# Revit family: 81MEJE-81MGJE-81MFJE-81MHJE_MC Chair_Mesh Seat No Pad Back With Armrest Silver Frame Black Shell_1
name_source: partatom
category: Furniture
revit_build: Autodesk Revit 2017 (Build: 20160225_1515(x64)
units: mm (PartAtom-declared; Revit-internal decimal feet)

## family parameters
Always vertical = Yes
Cut with Voids When Loaded = No
OmniClass Number = 23.40.20.00
OmniClass Title = General Furniture and Specialties
Room Calculation Point = No
Shared = No
Work Plane-Based = No

## types (48) — shared parameters
Assembly Code = E2020200
Caster = okm_G155
D = 580 mm  [stored 1.90289 ft]
Frame = okm_silver FX4
H = 850 mm  [stored 2.78871 ft]
Keynote = 12490
Kind = Chair
Manufacturer = Okamura Corporation
Product Categories = Multi-Purpose Chair
Shell & Armrest = okm_G721
URL = http://www.okamura.co.jp
W = 596 mm  [stored 1.95538 ft]

## per-type parameters (varying)
| type | Product Number | Seat |
| F1C2(White)_Without Brake Hard Caster | 81MEJE | okm_F1C2 |
| F1C7(Beige)_Without Brake Hard Caster | 81MEJE | okm_F1C7 |
| F1C8(Dark Brown)_Without Brake Hard Caster | 81MEJE | okm_F1C8 |
| F1C3(Light Gray)_Without Brake Hard Caster | 81MEJE | okm_F1C3 |
| F1D2(Medium Gray)_Without Brake Hard Caster | 81MEJE | okm_F1D2 |
| F1C1(Black)_Without Brake Hard Caster | 81MEJE | okm_F1C1 |
| F1C0(Purple)_Without Brake Hard Caster | 81MEJE | okm_F1C0 |
| F1C4(Dark Blue)_Without Brake Hard Caster | 81MEJE | okm_F1C4 |
| F1C6(Sage)_Without Brake Hard Caster | 81MEJE | okm_F1C6 |
| F1D5(Dark Green)_Without Brake Hard Caster | 81MEJE | okm_F1D5 |
| F1D8(Orange Red)_Without Brake Hard Caster | 81MEJE | okm_F1D8 |
| F1C9(Red)_Without Brake Hard Caster | 81MEJE | okm_F1C9 |
| F1C2(White)_With Brake Hard Caster | 81MFJE | okm_F1C2 |
| F1C7(Beige)_With Brake Hard Caster | 81MFJE | okm_F1C7 |
| F1C8(Dark Brown)_With Brake Hard Caster | 81MFJE | okm_F1C8 |
| F1C3(Light Gray)_With Brake Hard Caster | 81MFJE | okm_F1C3 |
| F1D2(Medium Gray)_With Brake Hard Caster | 81MFJE | okm_F1D2 |
| F1C1(Black)_With Brake Hard Caster | 81MFJE | okm_F1C1 |
| F1C0(Purple)_With Brake Hard Caster | 81MFJE | okm_F1C0 |
| F1C4(Dark Blue)_With Brake Hard Caster | 81MFJE | okm_F1C4 |
| F1C6(Sage)_With Brake Hard Caster | 81MFJE | okm_F1C6 |
| F1D5(Dark Green)_With Brake Hard Caster | 81MFJE | okm_F1D5 |
| F1D8(Orange Red)_With Brake Hard Caster | 81MFJE | okm_F1D8 |
| F1C9(Red)_With Brake Hard Caster | 81MFJE | okm_F1C9 |
| F1C2(White)_Without Brake Soft Caster | 81MGJE | okm_F1C2 |
| F1C7(Beige)_Without Brake Soft Caster | 81MGJE | okm_F1C7 |
| F1C8(Dark Brown)_Without Brake Soft Caster | 81MGJE | okm_F1C8 |
| F1C3(Light Gray)_Without Brake Soft Caster | 81MGJE | okm_F1C3 |
| F1D2(Medium Gray)_Without Brake Soft Caster | 81MGJE | okm_F1D2 |
| F1C1(Black)_Without Brake Soft Caster | 81MGJE | okm_F1C1 |
| F1C0(Purple)_Without Brake Soft Caster | 81MGJE | okm_F1C0 |
| F1C4(Dark Blue)_Without Brake Soft Caster | 81MGJE | okm_F1C4 |
| F1C6(Sage)_Without Brake Soft Caster | 81MGJE | okm_F1C6 |
| F1D5(Dark Green)_Without Brake Soft Caster | 81MGJE | okm_F1D5 |
| F1D8(Orange Red)_Without Brake Soft Caster | 81MGJE | okm_F1D8 |
| F1C9(Red)_Without Brake Soft Caster | 81MGJE | okm_F1C9 |
| F1C2(White)_With Brake Soft Caster | 81MHJE | okm_F1C2 |
| F1C7(Beige)_With Brake Soft Caster | 81MHJE | okm_F1C7 |
| F1C8(Dark Brown)_With Brake Soft Caster | 81MHJE | okm_F1C8 |
| F1C3(Light Gray)_With Brake Soft Caster | 81MHJE | okm_F1C3 |
| F1D2(Medium Gray)_With Brake Soft Caster | 81MHJE | okm_F1D2 |
| F1C1(Black)_With Brake Soft Caster | 81MHJE | okm_F1C1 |
| F1C0(Purple)_With Brake Soft Caster | 81MHJE | okm_F1C0 |
| F1C4(Dark Blue)_With Brake Soft Caster | 81MHJE | okm_F1C4 |
| F1C6(Sage)_With Brake Soft Caster | 81MHJE | okm_F1C6 |
| F1D5(Dark Green)_With Brake Soft Caster | 81MHJE | okm_F1D5 |
| F1D8(Orange Red)_With Brake Soft Caster | 81MHJE | okm_F1D8 |
| F1C9(Red)_With Brake Soft Caster | 81MHJE | okm_F1C9 |

note: [stored X ft] marks values corroborated as IEEE doubles in the binary element streams (Revit-internal decimal feet)
